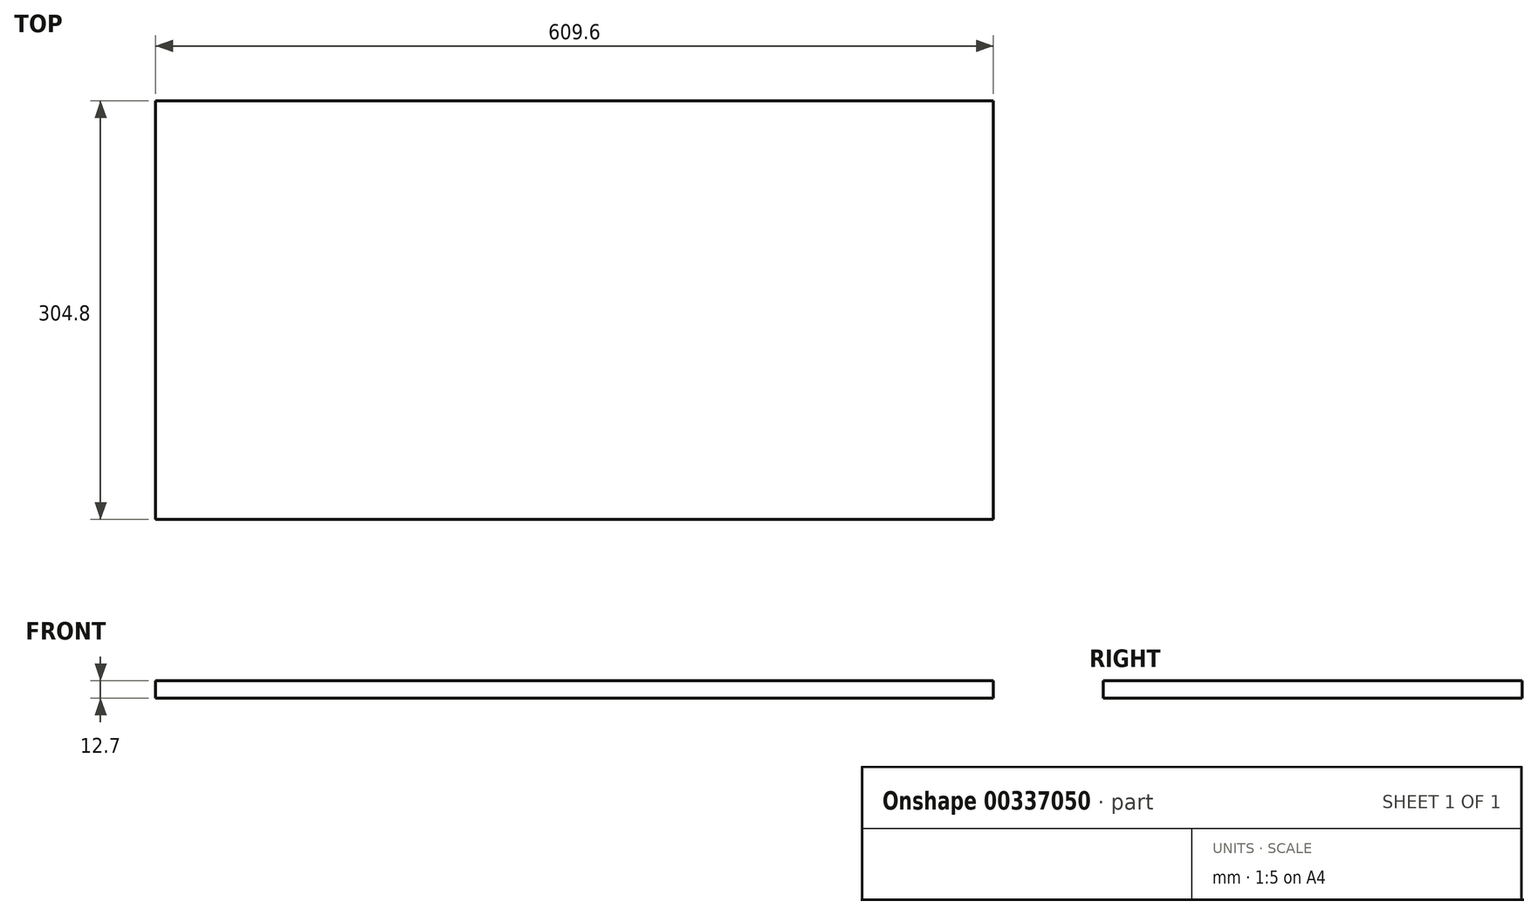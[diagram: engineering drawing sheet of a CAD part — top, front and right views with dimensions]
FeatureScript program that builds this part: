
annotation { "Feature Type Name" : "Feature", "Feature Type Description" : "" }
export const myFeature = defineFeature(function(context is Context, id is Id, definition is map)
    precondition{}
    {
        {
            var Q0;
            Q0=qCreatedBy(makeId("Top.planeOp"),FACE);
            var sketch = newSketch(context, id + "F0", { "sketchPlane" : qUnion([Q0])});
            skLineSegment(sketch, "E0.bottom", {"start": v(-306.86, 256.25) * mm, "end": v(302.74, 256.25) * mm});
            skLineSegment(sketch, "E0.top", {"start": v(-306.86, -48.55) * mm, "end": v(302.74, -48.55) * mm});
            skLineSegment(sketch, "E0.left", {"start": v(-306.86, 256.25) * mm, "end": v(-306.86, -48.55) * mm});
            skLineSegment(sketch, "E0.right", {"start": v(302.74, 256.25) * mm, "end": v(302.74, -48.55) * mm});
            skSolve(sketch);
        }
        {
            var Q0;
            Q0 = qSketchRegion(id + "F0", true);
            extrude(context, id + "F1", {"entities" : qUnion([Q0]), "depth" : 12.7 * mm});
        }
    });
